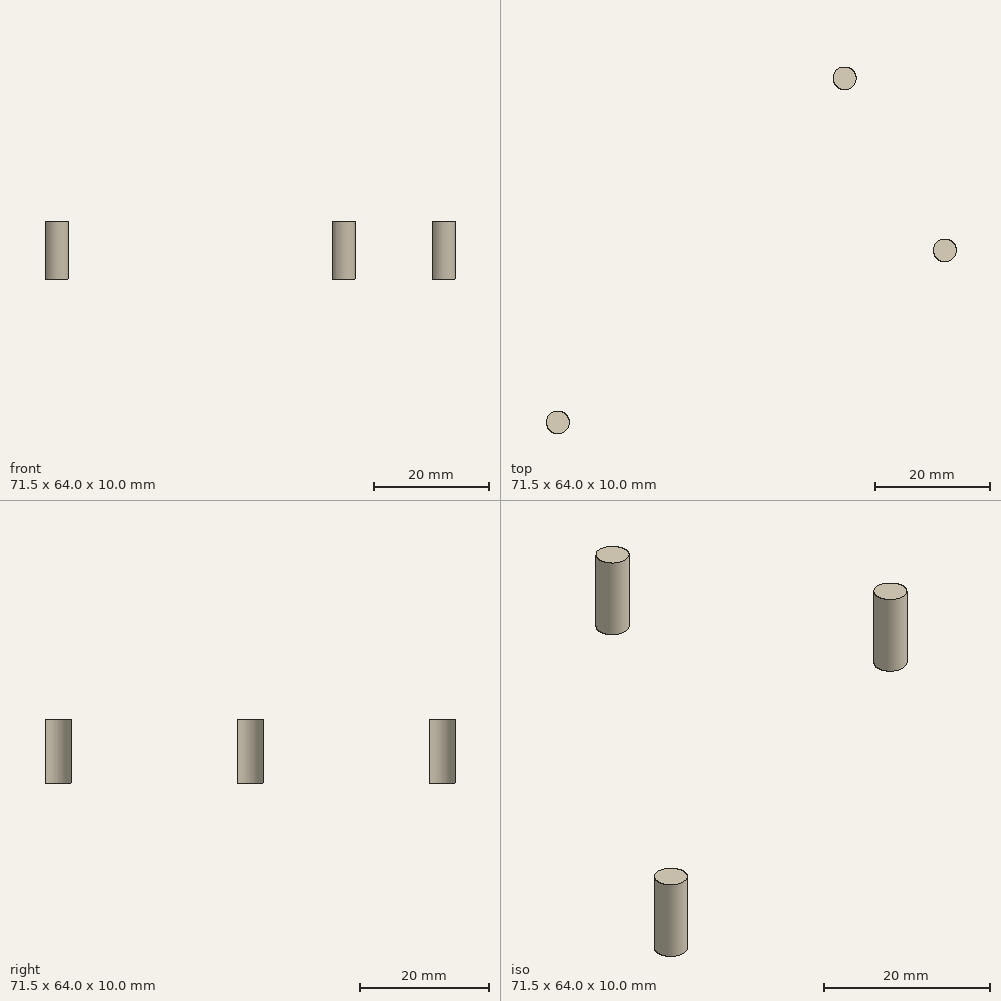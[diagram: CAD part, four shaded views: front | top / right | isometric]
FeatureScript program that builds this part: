
annotation { "Feature Type Name" : "Feature", "Feature Type Description" : "" }
export const myFeature = defineFeature(function(context is Context, id is Id, definition is map)
    precondition{}
    {
        {
            var Q0;
            Q0=qCreatedBy(makeId("Top.planeOp"),FACE);
            var sketch = newSketch(context, id + "F0", { "sketchPlane" : qUnion([Q0])});
            skLineSegment(sketch, "E0.bottom", {"start": v(-73.94, 29.86) * mm, "end": v(46.06, 29.86) * mm});
            skLineSegment(sketch, "E0.top", {"start": v(-73.94, -50.14) * mm, "end": v(46.06, -50.14) * mm});
            skLineSegment(sketch, "E0.left", {"start": v(-73.94, 29.86) * mm, "end": v(-73.94, -50.14) * mm});
            skLineSegment(sketch, "E0.right", {"start": v(46.06, 29.86) * mm, "end": v(46.06, -50.14) * mm});
            skSolve(sketch);
        }
        {
            var Q0;
            Q0=makeQuery(id+"F0.imprint","IMPRINT",FACE,{"disambiguationData":[TD([[makeQuery(id+"F0.imprint","IMPRINT",EDGE,{"derivedFrom":sQuery(id+"F0.wireOp",EDGE,"E0.bottom")}),-1.0]])]});
            extrude(context, id + "F1", {"entities" : qUnion([Q0]), "depth" : 10 * mm});
        }
        {
            var Q0;
            Q0=makeQuery(id+"F1.opExtrude","CAP_FACE",FACE,{"disambiguationData":[OSD([sQuery(id+"F0.wireOp",EDGE,"E0.bottom"),sQuery(id+"F0.wireOp",EDGE,"E0.top"),sQuery(id+"F0.wireOp",EDGE,"E0.left"),sQuery(id+"F0.wireOp",EDGE,"E0.right")])],"isStart":false});
            var sketch = newSketch(context, id + "F2", { "sketchPlane" : qUnion([Q0])});
            skLineSegment(sketch, "E1", {"start": v(-13.94, 29.86) * mm, "end": v(-13.94, -58.6) * mm, "construction": true});
            skCircle(sketch, "E2", {"center": v(-38.94, 19.86) * mm, "radius": 2 * mm});
            skLineSegment(sketch, "E3", {"start": v(-73.94, -10.14) * mm, "end": v(54.04, -10.14) * mm, "construction": true});
            skPoint(sketch, "E3.endSnap0", {"position": v(46.06, -10.14) * mm});
            skCircle(sketch, "E4.MirrorC", {"center": v(11.06, 19.86) * mm, "radius": 2 * mm});
            skCircle(sketch, "E5.MirrorC", {"center": v(-38.94, -40.14) * mm, "radius": 2 * mm});
            skCircle(sketch, "E6.MirrorC", {"center": v(11.06, -40.14) * mm, "radius": 2 * mm});
            skCircle(sketch, "E7", {"center": v(-56.44, -10.14) * mm, "radius": 2 * mm});
            skCircle(sketch, "E8.MirrorC", {"center": v(28.56, -10.14) * mm, "radius": 2 * mm});
            skSolve(sketch);
        }
        {
            var Q0;
            Q0=makeQuery(id+"F2.imprint","IMPRINT",FACE,{"disambiguationData":[TD([[makeQuery(id+"F2.imprint","IMPRINT",EDGE,{"derivedFrom":sQuery(id+"F2.wireOp",EDGE,"E2")}),1.0]])]});
            var Q1;
            Q1=makeQuery(id+"F2.imprint","IMPRINT",FACE,{"disambiguationData":[TD([[makeQuery(id+"F2.imprint","IMPRINT",EDGE,{"derivedFrom":sQuery(id+"F2.wireOp",EDGE,"E7")}),1.0]])]});
            var Q2;
            Q2=makeQuery(id+"F2.imprint","IMPRINT",FACE,{"disambiguationData":[TD([[makeQuery(id+"F2.imprint","IMPRINT",EDGE,{"derivedFrom":sQuery(id+"F2.wireOp",EDGE,"E5.MirrorC")}),-1.0]])]});
            var Q3;
            Q3=makeQuery(id+"F2.imprint","IMPRINT",FACE,{"disambiguationData":[TD([[makeQuery(id+"F2.imprint","IMPRINT",EDGE,{"derivedFrom":sQuery(id+"F2.wireOp",EDGE,"E6.MirrorC")}),1.0]])]});
            var Q4;
            Q4=makeQuery(id+"F2.imprint","IMPRINT",FACE,{"disambiguationData":[TD([[makeQuery(id+"F2.imprint","IMPRINT",EDGE,{"derivedFrom":sQuery(id+"F2.wireOp",EDGE,"E8.MirrorC")}),-1.0]])]});
            var Q5;
            Q5=makeQuery(id+"F2.imprint","IMPRINT",FACE,{"disambiguationData":[TD([[makeQuery(id+"F2.imprint","IMPRINT",EDGE,{"derivedFrom":sQuery(id+"F2.wireOp",EDGE,"E4.MirrorC")}),-1.0]])]});
            extrude(context, id + "F3", {"entities" : qUnion([Q0, Q1, Q2, Q3, Q4, Q5]), "operationType" : NewBodyOperationType.REMOVE, "endBound" : BoundingType.THROUGH_ALL, "oppositeDirection" : true, "depth" : 25 * mm});
        }
    });
